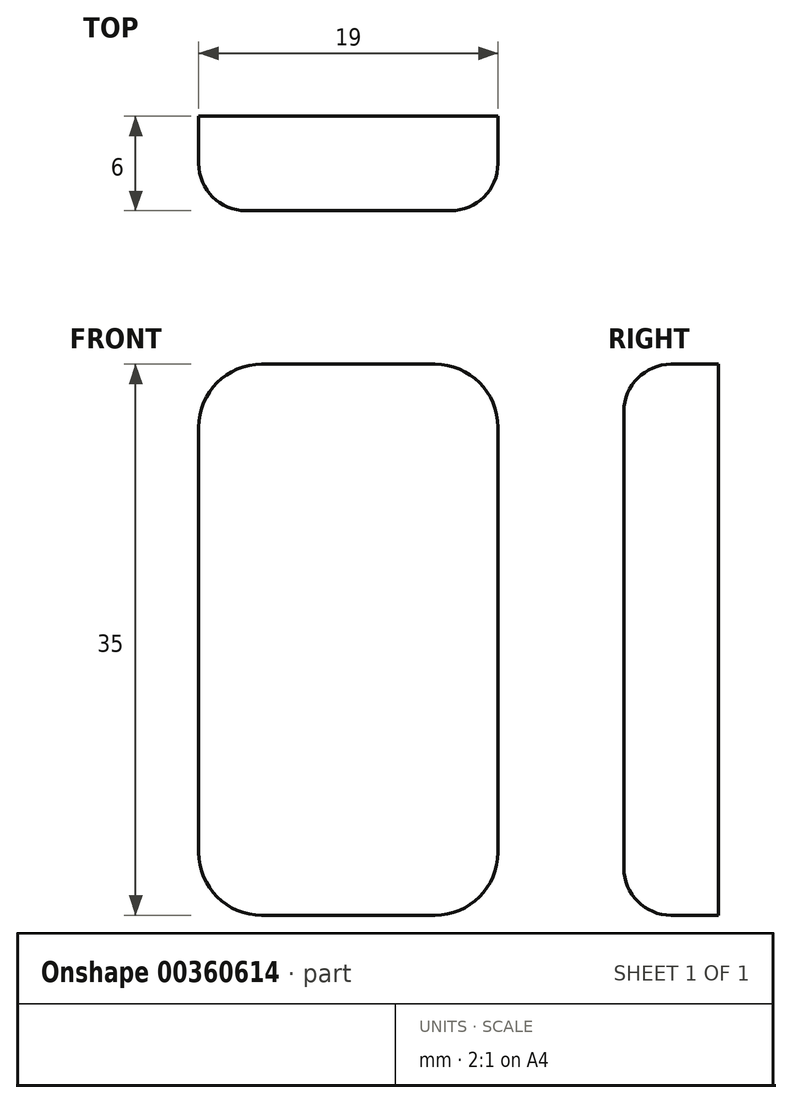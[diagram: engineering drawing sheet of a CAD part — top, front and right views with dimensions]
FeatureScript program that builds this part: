
annotation { "Feature Type Name" : "Feature", "Feature Type Description" : "" }
export const myFeature = defineFeature(function(context is Context, id is Id, definition is map)
    precondition{}
    {
        {
            var Q0;
            Q0=qCreatedBy(makeId("Front.planeOp"),FACE);
            var sketch = newSketch(context, id + "F0", { "sketchPlane" : qUnion([Q0])});
            skLineSegment(sketch, "E0.bottom", {"start": v(4.96, -0.18) * mm, "end": v(-14.04, -0.18) * mm});
            skLineSegment(sketch, "E0.top", {"start": v(4.96, 34.82) * mm, "end": v(-14.04, 34.82) * mm});
            skLineSegment(sketch, "E0.left", {"start": v(4.96, -0.18) * mm, "end": v(4.96, 34.82) * mm});
            skLineSegment(sketch, "E0.right", {"start": v(-14.04, -0.18) * mm, "end": v(-14.04, 34.82) * mm});
            skPoint(sketch, "E0.middle", {"position": v(-4.54, 17.32) * mm});
            skSolve(sketch);
        }
        {
            var Q0;
            Q0 = qSketchRegion(id + "F0", true);
            extrude(context, id + "F1", {"entities" : qUnion([Q0]), "depth" : 6 * mm});
        }
        {
            var Q0;
            Q0=makeQuery(id+"F1.opExtrude","SWEPT_EDGE",EDGE,{"disambiguationData":[OSD([sQuery(id+"F0.wireOp",EDGE,"E0.top"),sQuery(id+"F0.wireOp",EDGE,"E0.left")])]});
            var Q1;
            Q1=makeQuery(id+"F1.opExtrude","SWEPT_EDGE",EDGE,{"disambiguationData":[OSD([sQuery(id+"F0.wireOp",EDGE,"E0.bottom"),sQuery(id+"F0.wireOp",EDGE,"E0.left")])]});
            var Q2;
            Q2=makeQuery(id+"F1.opExtrude","SWEPT_EDGE",EDGE,{"disambiguationData":[OSD([sQuery(id+"F0.wireOp",EDGE,"E0.top"),sQuery(id+"F0.wireOp",EDGE,"E0.right")])]});
            var Q3;
            Q3=makeQuery(id+"F1.opExtrude","SWEPT_EDGE",EDGE,{"disambiguationData":[OSD([sQuery(id+"F0.wireOp",EDGE,"E0.bottom"),sQuery(id+"F0.wireOp",EDGE,"E0.right")])]});
            fillet(context, id + "F2", {"entities" : qUnion([Q0, Q1, Q2, Q3]), "radius" : 4 * mm, "tangentPropagation" : true, "allowEdgeOverflow" : false});
        }
        {
            var Q0;
            Q0=makeQuery(id+"F1.opExtrude","CAP_EDGE",EDGE,{"disambiguationData":[OSD([sQuery(id+"F0.wireOp",EDGE,"E0.right")])],"isStart":false});
            fillet(context, id + "F3", {"entities" : qUnion([Q0]), "radius" : 3 * mm, "tangentPropagation" : true, "allowEdgeOverflow" : false});
        }
    });
